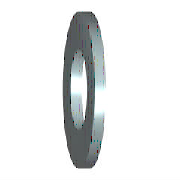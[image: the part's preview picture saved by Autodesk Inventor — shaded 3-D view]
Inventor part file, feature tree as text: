
AUTODESK INVENTOR PART (.ipt)
format: ipt  version: 2015 (Build 190159000, 159)  size: 105,984 bytes
history: native  units: mm (DEFAULTED — no unit token found)
features: other x1, plane x1, sketch x1
ambient origin geometry x7: Origin, YZ Plane, XY Plane, X Axis, Y Axis, Z Axis, Center Point
bodies: Solid1 (feature_tree), Body (feature_tree)
feature tree (3):
  other  "Work Axis1"
  plane  "Work Plane1"
  sketch  "Sketch"  dims[d0=8.4mm d1=16.0mm d2=1.6mm d3=0.0mm d4=0.0mm d5=0.0mm d6=0.0mm d7=0.0mm]
